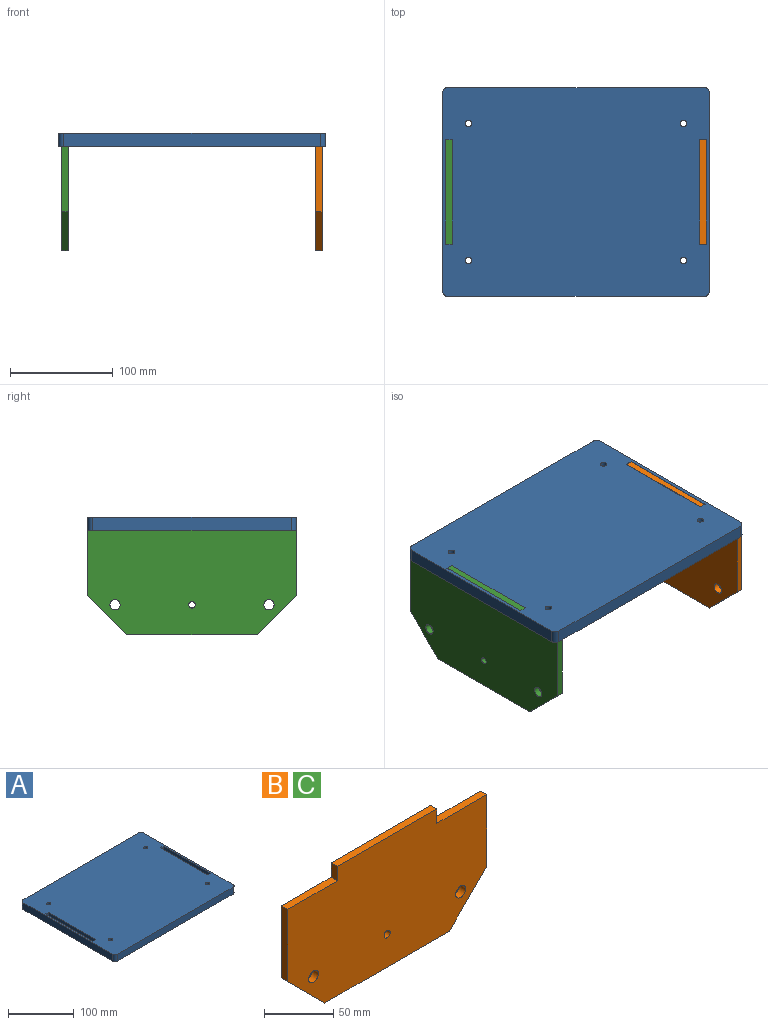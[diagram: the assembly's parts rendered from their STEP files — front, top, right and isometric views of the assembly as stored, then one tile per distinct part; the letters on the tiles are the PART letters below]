
ASSEMBLY  parts=3 mates=3
PART A: 22 faces, bbox 260.4x203.2x12.7 mm
  f0: plane 260.35x203.2mm, normal (0,0,1), area 51458.8mm2, adj f2,f3,f4,f5,f6,f7,f8,f9
  f1: plane 260.35x203.2mm, normal (0,0,-1), area 51458.8mm2, adj f2,f3,f4,f5,f6,f7,f8,f9
  f2: plane 250.19x12.7mm, normal (0,1,0), area 3177.4mm2, adj f0,f1,f18,f21
  f3: plane 193.04x12.7mm, normal (-1,0,0), area 2451.6mm2, adj f0,f1,f18,f19
  f4: plane 250.19x12.7mm, normal (0,-1,0), area 3177.4mm2, adj f0,f1,f19,f20
  f5: plane 193.04x12.7mm, normal (1,0,0), area 2451.6mm2, adj f0,f1,f20,f21
  f6: cylinder r=3.17mm len=12.7mm, axis (0,0,1), area 253.4mm2, adj f0,f1
  f7: cylinder r=3.17mm len=12.7mm, axis (0,0,1), area 253.4mm2, adj f0,f1
  f8: cylinder r=3.17mm len=12.7mm, axis (0,0,1), area 253.4mm2, adj f0,f1
  f9: cylinder r=3.17mm len=12.7mm, axis (0,0,1), area 253.4mm2, adj f0,f1
  f10: plane 12.7x6.38mm, normal (0,-1,0), area 81mm2, adj f0,f1,f11,f13
  f11: plane 101.6x12.7mm, normal (1,0,0), area 1290.3mm2, adj f0,f1,f10,f12
  f12: plane 12.7x6.38mm, normal (0,1,0), area 81mm2, adj f0,f1,f11,f13
  f13: plane 101.6x12.7mm, normal (-1,0,0), area 1290.3mm2, adj f0,f1,f10,f12
  f14: plane 101.6x12.7mm, normal (-1,0,0), area 1290.3mm2, adj f0,f1,f15,f17
  f15: plane 12.7x6.38mm, normal (0,-1,0), area 81mm2, adj f0,f1,f14,f16
  f16: plane 101.6x12.7mm, normal (1,0,0), area 1290.3mm2, adj f0,f1,f15,f17
  f17: plane 12.7x6.38mm, normal (0,1,0), area 81mm2, adj f0,f1,f14,f16
  f18: cylinder r=5.08mm len=12.7mm, axis (0,0,1), area 101.3mm2, adj f0,f1,f2,f3
  f19: cylinder r=5.08mm len=12.7mm, axis (0,0,-1), area 101.3mm2, adj f0,f1,f3,f4
  f20: cylinder r=5.08mm len=12.7mm, axis (0,0,1), area 101.3mm2, adj f0,f1,f4,f5
  f21: cylinder r=5.08mm len=12.7mm, axis (0,0,-1), area 101.3mm2, adj f0,f1,f2,f5
PART B: 15 faces, bbox 203.2x6.4x114.3 mm
  f0: plane 50.8x6.35mm, normal (0,0,1), area 322.6mm2, adj f1,f7,f8,f9
  f1: plane 63.5x6.35mm, normal (-1,0,0), area 403.2mm2, adj f0,f8,f9,f14
  f2: plane 127x6.35mm, normal (0,0,-1), area 806.5mm2, adj f8,f9,f13,f14
  f3: plane 63.5x6.35mm, normal (1,0,0), area 403.2mm2, adj f4,f8,f9,f13
  f4: plane 50.8x6.35mm, normal (0,0,1), area 322.6mm2, adj f3,f5,f8,f9
  f5: plane 12.7x6.35mm, normal (1,0,0), area 80.6mm2, adj f4,f6,f8,f9
  f6: plane 101.6x6.35mm, normal (0,0,1), area 645.2mm2, adj f5,f7,f8,f9
  f7: plane 12.7x6.35mm, normal (-1,0,0), area 80.6mm2, adj f0,f6,f8,f9
  f8: plane 203.2x114.3mm, normal (0,-1,0), area 20295.1mm2, adj f0,f1,f2,f3,f4,f5,f6,f7
  f9: plane 203.2x114.3mm, normal (0,1,0), area 20295.1mm2, adj f0,f1,f2,f3,f4,f5,f6,f7
  f10: cylinder r=3.17mm len=6.35mm, axis (0,-1,0), area 126.7mm2, adj f8,f9
  f11: cylinder r=5mm len=10mm, axis (0,-1,0), area 199.5mm2, adj f8,f9
  f12: cylinder r=5mm len=10mm, axis (0,-1,0), area 199.5mm2, adj f8,f9
  f13: plane 38.1x38.1mm, normal (0.71,0,-0.71), area 342.1mm2, adj f2,f3,f8,f9
  f14: plane 38.1x38.1mm, normal (-0.71,0,-0.71), area 342.1mm2, adj f1,f2,f8,f9
PART C: same geometry as B
PLACE A rot(axis=(0.39,-0.66,0.64),0deg) t=(-0.37,57.23,-35.31)mm
PLACE B rot(axis=(0,0,-1),90deg) t=(126.35,57.23,-86.11)mm
PLACE C rot(axis=(0,0,1),90deg) t=(-127.37,57.23,-86.11)mm
MATE pin_slot A.f14 <-> C.f8  axis (-1,0,0) through (-121.02,57.23,-28.96)mm
MATE planar C.f0 <-> A.f1  axis (0,0,1) through (-124.19,-18.97,-35.31)mm
MATE planar C.f7 <-> A.f17  axis (0,-1,0) through (-124.19,6.43,-28.96)mm
